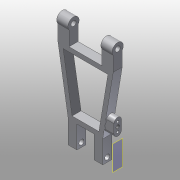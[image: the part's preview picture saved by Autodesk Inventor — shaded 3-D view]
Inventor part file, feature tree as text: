
AUTODESK INVENTOR PART (.ipt)
format: ipt  version: 2015 (Build 190159000, 159)  size: 155,648 bytes
history: native  units: mm
features: sketch x9, other x3, plane x1
ambient origin geometry x8: Origin, YZ Plane, XZ Plane, XY Plane, X Axis, Y Axis, Z Axis, Center Point
bodies: Solid1 (feature_tree)
feature tree (13):
  other  "500-006.ipt"
  other  "Solid1::500-006.ipt"
  other  "TaggingFeature1"
  sketch  "Sketch1"  dims[d0=10.0mm]
  sketch  "Sketch2"
  sketch  "Sketch3"
  sketch  "Sketch4"
  sketch  "Sketch5"
  sketch  "Sketch6"
  sketch  "Sketch7"
  sketch  "Sketch8"
  sketch  "Sketch9"
  plane  "Work Plane1"
